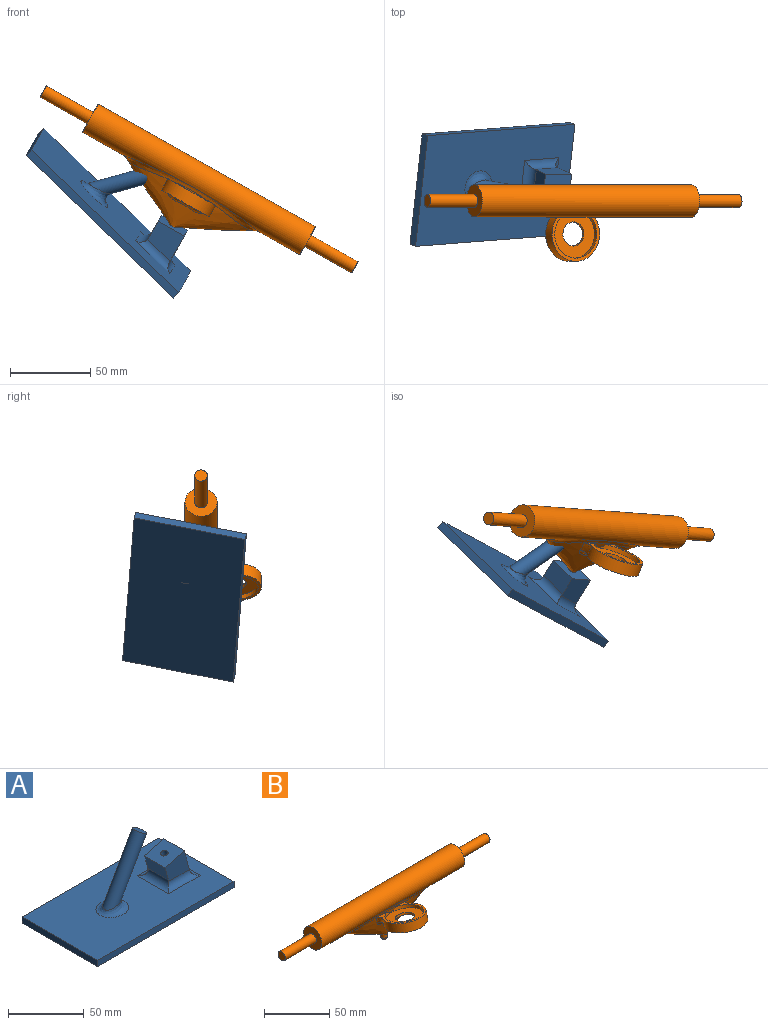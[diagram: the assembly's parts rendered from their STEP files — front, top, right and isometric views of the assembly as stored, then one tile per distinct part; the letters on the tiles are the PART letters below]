
ASSEMBLY  parts=2 mates=1
PART A: 22 faces, bbox 127.5x70.4x57.9 mm
  f0: plane 70.43x5mm, normal (1,0,0), area 352.1mm2, adj f1,f3,f4,f5
  f1: plane 127.5x5mm, normal (0,1,0), area 637.5mm2, adj f0,f2,f4,f5
  f2: plane 70.43x5mm, normal (-1,0,0), area 352.1mm2, adj f1,f3,f4,f5
  f3: plane 127.5x5mm, normal (0,-1,0), area 637.5mm2, adj f0,f2,f4,f5
  f4: plane 127.5x70.43mm, normal (0,0,1), area 7756.9mm2, adj f0,f1,f2,f3,f17,f18,f19,f20
  f5: plane 127.5x70.43mm, normal (0,0,-1), area 8978.5mm2, adj f0,f1,f2,f3,f13,f14
  f6: plane 19.41x18.92mm, normal (0.97,0,0.26), area 373.6mm2, adj f7,f9,f11,f18,f19,f20
  f7: plane 22.72x17.62mm, normal (0,1,0), area 293.4mm2, adj f6,f8,f11,f20,f21
  f8: plane 19.07x11.5mm, normal (-0.97,0,-0.26), area 227.1mm2, adj f7,f9,f11,f21
  f9: plane 22.72x17.62mm, normal (0,-1,0), area 293.4mm2, adj f6,f8,f11,f19,f21
  f10: cylinder r=2.5mm len=22.16mm, axis (-0.26,0,0.97), area 328.6mm2, adj f11,f12
  f11: plane 19.07x18mm, normal (-0.26,0,0.97), area 335.7mm2, adj f6,f7,f8,f9,f10
  f12: plane 5.18x5mm, normal (0,0,1), area 20.3mm2, adj f10
  f13: cylinder r=5mm len=4.52mm, axis (-0.49,0,-0.87), area 1mm2, adj f5,f14
  f14: cone r=5mm half-angle=60.6deg, axis (-0.49,0,-0.87), area 1mm2, adj f5,f13
  f15: plane 10x8.71mm, normal (0.49,0,0.87), area 78.5mm2, adj f16
  f16: cylinder r=5mm len=55.03mm, axis (-0.49,0,-0.87), area 1630.5mm2, adj f15,f17
  f17: bspline ~22.94x19.99mm, area 373.4mm2, adj f4,f16
  f18: cylinder r=5mm len=29.07mm, axis (0,1,0), area 153.2mm2, adj f4,f6,f19,f20
  f19: cylinder r=5mm len=29.64mm, axis (1,0,0), area 182.7mm2, adj f4,f6,f9,f18,f21
  f20: cylinder r=5mm len=29.64mm, axis (-1,0,0), area 182.7mm2, adj f4,f6,f7,f18,f21
  f21: cylinder r=5mm len=29.07mm, axis (0,-1,0), area 203.3mm2, adj f4,f7,f8,f9,f19,f20
PART B: 23 faces, bbox 224.6x52.7x51.8 mm
  f0: bspline ~110.19x33.92mm, area 2740.2mm2, adj f9,f10,f20,f21,f22
  f1: cylinder r=4mm len=33.63mm, axis (-1,0,0), area 845.1mm2, adj f2,f4
  f2: plane 8x8mm, normal (1,0,0), area 50.3mm2, adj f1
  f3: cylinder r=10mm len=155mm, axis (-1,0,0), area 7988.3mm2, adj f4,f5,f9
  f4: plane 20x20mm, normal (1,0,0), area 263.9mm2, adj f1,f3
  f5: plane 20x20mm, normal (-1,0,0), area 263.9mm2, adj f3,f7
  f6: plane 8x8mm, normal (-1,0,0), area 50.3mm2, adj f7
  f7: cylinder r=4mm len=33.63mm, axis (-1,0,0), area 845.1mm2, adj f5,f6
  f8: bspline ~31.91x2.55mm, area -13.2mm2, adj f9,f15,f18
  f9: bspline ~99.5x18.37mm, area 767.7mm2, adj f0,f3,f8,f18,f20,f22
  f10: cylinder r=2.5mm len=5mm, axis (0,0,1), area 47.1mm2, adj f0,f11
  f11: sphere r=2.5mm, area 39.3mm2, adj f10
  f12: plane 30x29.27mm, normal (0,-0.22,-0.98), area 530.1mm2, adj f13,f17
  f13: cylinder r=7.5mm len=15.07mm, axis (0,0.22,0.98), area 94.2mm2, adj f12,f14
  f14: plane 30x29.27mm, normal (0,0.22,0.98), area 530.1mm2, adj f13,f15
  f15: cylinder r=15mm len=30mm, axis (0,-0.22,-0.98), area 266.6mm2, adj f8,f14,f18
  f16: cylinder r=17mm len=34mm, axis (0,-0.22,-0.98), area 615.2mm2, adj f18,f19,f20,f22
  f17: cylinder r=15mm len=30mm, axis (0,-0.22,-0.98), area 282.7mm2, adj f12,f19
  f18: plane 34.14x30.9mm, normal (0,0.22,0.98), area 189.3mm2, adj f8,f9,f15,f16,f20,f22
  f19: plane 36.34x35.52mm, normal (0,-0.22,-0.98), area 201.1mm2, adj f16,f17,f21
  f20: bspline ~12.21x9.68mm, area 52.1mm2, adj f0,f9,f16,f18,f21
  f21: bspline ~27.89x5.9mm, area 93mm2, adj f0,f19,f20,f22
  f22: bspline ~12.32x9.61mm, area 52.1mm2, adj f0,f9,f16,f18,f21
PLACE A rot(axis=(0.28,0.96,-0.04),46.1deg) t=(-50.72,86.08,-20.67)mm
PLACE B rot(axis=(0.39,0.92,-0.1),32deg) t=(7.29,75.27,2.03)mm
MATE ball A.f10 <-> B.f10  axis (0.48,-0.22,0.85) through (-8.98,82.68,-26.8)mm
